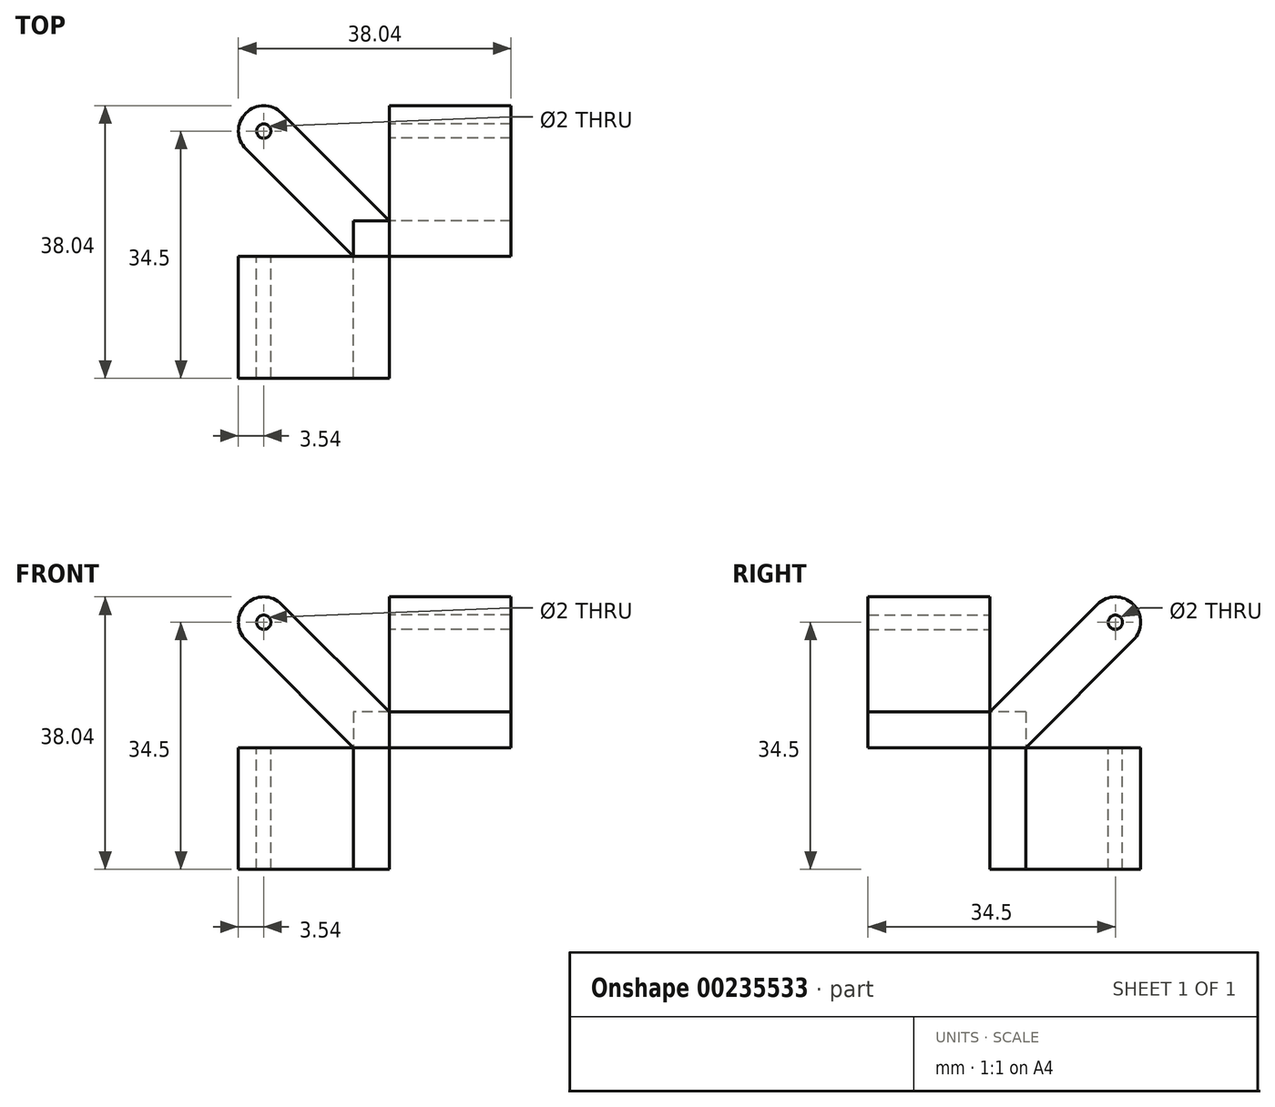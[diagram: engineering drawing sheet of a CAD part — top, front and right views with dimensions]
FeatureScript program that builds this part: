
annotation { "Feature Type Name" : "Feature", "Feature Type Description" : "" }
export const myFeature = defineFeature(function(context is Context, id is Id, definition is map)
    precondition{}
    {
        {
            var Q0;
            Q0=qCreatedBy(makeId("Front.planeOp"),FACE);
            var sketch = newSketch(context, id + "F0", { "sketchPlane" : qUnion([Q0])});
            skLineSegment(sketch, "E0.bottom", {"start": v(0, 0) * mm, "end": v(-5, 0) * mm});
            skLineSegment(sketch, "E0.left", {"start": v(0, 0) * mm, "end": v(0, 5) * mm});
            skLineSegment(sketch, "E1", {"start": v(-5, 0) * mm, "end": v(-20, 15) * mm});
            skLineSegment(sketch, "E2", {"start": v(0, 5) * mm, "end": v(-15, 20) * mm});
            skArc(sketch, "E3", {"start": v(-15, 20) * mm, "mid": v(-20, 20) * mm, "end": v(-20, 15) * mm});
            skCircle(sketch, "E4", {"center": v(-17.5, 17.5) * mm, "radius": 1 * mm});
            skSolve(sketch);
        }
        {
            var Q0;
            Q0 = qSketchRegion(id + "F0", true);
            extrude(context, id + "F1", {"entities" : qUnion([Q0]), "depth" : 17 * mm});
        }
        {
            var Q0;
            Q0=makeQuery(id+"F1.opExtrude","CAP_FACE",FACE,{"disambiguationData":[OSD([sQuery(id+"F0.wireOp",EDGE,"E0.left"),sQuery(id+"F0.wireOp",EDGE,"E0.bottom"),sQuery(id+"F0.wireOp",EDGE,"E1"),sQuery(id+"F0.wireOp",EDGE,"E2"),sQuery(id+"F0.wireOp",EDGE,"E3"),sQuery(id+"F0.wireOp",EDGE,"E4")])],"isStart":true});
            var sketch = newSketch(context, id + "F2", { "sketchPlane" : qUnion([Q0])});
            skLineSegment(sketch, "E5.bottom", {"start": v(0, 5) * mm, "end": v(5, 5) * mm});
            skLineSegment(sketch, "E5.top", {"start": v(0, 0) * mm, "end": v(5, 0) * mm});
            skLineSegment(sketch, "E5.left", {"start": v(0, 5) * mm, "end": v(0, 0) * mm});
            skLineSegment(sketch, "E5.right", {"start": v(5, 5) * mm, "end": v(5, 0) * mm});
            skSolve(sketch);
        }
        {
            var Q0;
            Q0 = qSketchRegion(id + "F2", true);
            extrude(context, id + "F3", {"entities" : qUnion([Q0]), "operationType" : NewBodyOperationType.ADD, "depth" : 5 * mm});
        }
        {
            var Q0;
            Q0=makeQuery(id+"F3.boolean.opBoolean","MERGE",FACE,{"derivedFrom":[makeQuery(id+"F1.opExtrude","SWEPT_FACE",FACE,{"disambiguationData":[OSD([sQuery(id+"F0.wireOp",EDGE,"E0.left")])]}),makeQuery(id+"F3.opExtrude","SWEPT_FACE",FACE,{"disambiguationData":[OSD([sQuery(id+"F2.wireOp",EDGE,"E5.left")])]})]});
            var sketch = newSketch(context, id + "F4", { "sketchPlane" : qUnion([Q0])});
            skLineSegment(sketch, "E6.bottom", {"start": v(0, 0) * mm, "end": v(5, 0) * mm});
            skLineSegment(sketch, "E6.left", {"start": v(0, 0) * mm, "end": v(0, 5) * mm});
            skLineSegment(sketch, "E7", {"start": v(15, 20) * mm, "end": v(0, 5) * mm});
            skLineSegment(sketch, "E8", {"start": v(5, 0) * mm, "end": v(20, 15) * mm});
            skArc(sketch, "E9", {"start": v(20, 15) * mm, "mid": v(20, 20) * mm, "end": v(15, 20) * mm});
            skCircle(sketch, "E10", {"center": v(17.5, 17.5) * mm, "radius": 1 * mm});
            skSolve(sketch);
        }
        {
            var Q0;
            Q0 = qSketchRegion(id + "F4", true);
            extrude(context, id + "F5", {"entities" : qUnion([Q0]), "operationType" : NewBodyOperationType.ADD, "depth" : 17 * mm});
        }
        {
            var Q0;
            Q0=makeQuery(id+"F5.boolean.opBoolean","MERGE",FACE,{"derivedFrom":[makeQuery(id+"F3.boolean.opBoolean","MERGE",FACE,{"derivedFrom":[makeQuery(id+"F1.opExtrude","SWEPT_FACE",FACE,{"disambiguationData":[OSD([sQuery(id+"F0.wireOp",EDGE,"E0.bottom")])]}),makeQuery(id+"F3.opExtrude","SWEPT_FACE",FACE,{"disambiguationData":[OSD([sQuery(id+"F2.wireOp",EDGE,"E5.top")])]})]}),makeQuery(id+"F5.opExtrude","SWEPT_FACE",FACE,{"disambiguationData":[OSD([sQuery(id+"F4.wireOp",EDGE,"E6.bottom")])]})]});
            var sketch = newSketch(context, id + "F6", { "sketchPlane" : qUnion([Q0])});
            skLineSegment(sketch, "E11.bottom", {"start": v(0, 0) * mm, "end": v(-5, 0) * mm});
            skLineSegment(sketch, "E11.left", {"start": v(0, 0) * mm, "end": v(0, -5) * mm});
            skLineSegment(sketch, "E12", {"start": v(-15, -20) * mm, "end": v(0, -5) * mm});
            skLineSegment(sketch, "E13", {"start": v(-20, -15) * mm, "end": v(-5, 0) * mm});
            skArc(sketch, "E14", {"start": v(-20, -15) * mm, "mid": v(-20, -20) * mm, "end": v(-15, -20) * mm});
            skCircle(sketch, "E15", {"center": v(-17.5, -17.5) * mm, "radius": 1 * mm});
            skSolve(sketch);
        }
        {
            var Q0;
            Q0 = qSketchRegion(id + "F6", true);
            extrude(context, id + "F7", {"entities" : qUnion([Q0]), "operationType" : NewBodyOperationType.ADD, "depth" : 17 * mm});
        }
    });
